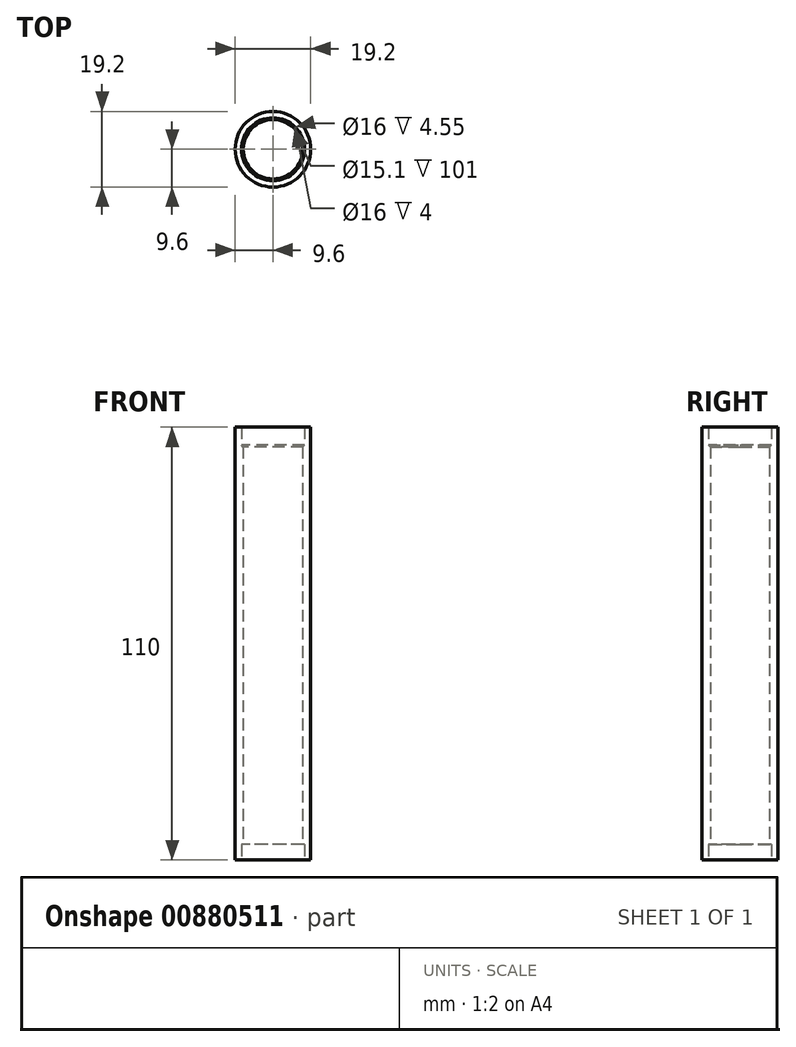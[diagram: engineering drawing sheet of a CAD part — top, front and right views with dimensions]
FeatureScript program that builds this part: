
annotation { "Feature Type Name" : "Feature", "Feature Type Description" : "" }
export const myFeature = defineFeature(function(context is Context, id is Id, definition is map)
    precondition{}
    {
        {
            var Q0;
            Q0=qCreatedBy(makeId("Top.planeOp"),FACE);
            var sketch = newSketch(context, id + "F0", { "sketchPlane" : qUnion([Q0])});
            skCircle(sketch, "E0", {"center": v(0, 0) * mm, "radius": 9.6 * mm});
            skCircle(sketch, "E1", {"center": v(0, 0) * mm, "radius": 8 * mm});
            skCircle(sketch, "E2", {"center": v(0, 0) * mm, "radius": 7.55 * mm});
            skSolve(sketch);
        }
        {
            var Q0;
            Q0 = qSketchRegion(id + "F0", true);
            extrude(context, id + "F1", {"entities" : qUnion([Q0]), "depth" : 110 * mm, "offsetDistance" : 25 * mm});
        }
        {
            var Q0;
            Q0=makeQuery(id+"F0.imprint","IMPRINT",FACE,{"disambiguationData":[TD([[makeQuery(id+"F0.imprint","IMPRINT",EDGE,{"derivedFrom":sQuery(id+"F0.wireOp",EDGE,"E1")}),1.0]])]});
            extrude(context, id + "F2", {"entities" : qUnion([Q0]), "operationType" : NewBodyOperationType.ADD, "depth" : 106 * mm, "offsetDistance" : 25 * mm});
        }
        {
            var Q0;
            Q0=makeQuery(id+"F0.imprint","IMPRINT",FACE,{"disambiguationData":[TD([[makeQuery(id+"F0.imprint","IMPRINT",EDGE,{"derivedFrom":sQuery(id+"F0.wireOp",EDGE,"E1")}),1.0]])]});
            extrude(context, id + "F3", {"entities" : qUnion([Q0]), "operationType" : NewBodyOperationType.REMOVE, "depth" : 4 * mm, "offsetDistance" : 25 * mm});
        }
        {
            var Q0;
            Q0=makeQuery(id+"F3.boolean.opBoolean","COPY",EDGE,{"derivedFrom":makeQuery(id+"F3.opExtrude","CAP_EDGE",EDGE,{"disambiguationData":[OSD([sQuery(id+"F0.wireOp",EDGE,"E2")])],"isStart":false})});
            var Q1;
            Q1=makeQuery(id+"F2.opExtrude","CAP_EDGE",EDGE,{"disambiguationData":[OSD([sQuery(id+"F0.wireOp",EDGE,"E2")])],"isStart":false});
            chamfer(context, id + "F4", {"entities" : qUnion([Q0, Q1]), "width" : 1 * mm, "tangentPropagation" : true});
        }
    });
